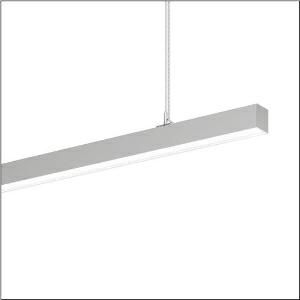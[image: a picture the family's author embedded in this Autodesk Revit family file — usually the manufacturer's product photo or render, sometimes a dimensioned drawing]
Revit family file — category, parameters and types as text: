
# Revit family: silica_21_51mx30tct9s
name_source: partatom
category: Lighting Fixtures
units: mm (PartAtom-declared; Revit-internal decimal feet)

## family parameters
Cut with Voids When Loaded = No
Host = Face
Light Source = No
Part Type = Normal
Room Calculation Point = No
Round Connector Dimension = Use Diameter
Shared = No

## types (1)
- --- (1 x LED, 10300 lm, 84.4 W, 6500K)
    Apparent Load = 84 VA
    CIE Flux Codes = 47 79 96 58 100
    Color Rendering = 80
    Color Temperature = 6500K
    Default Elevation = 1800 mm
    Description = Silica 21, office luminaire, primary optical cover: cover, of PMMA, opal, light emission: direct/indirect distribution, primary light characteristic: symmetric, installation type: suspended mounting, LED, rated luminous flux: 10.300lm, luminous efficacy: 116lm/W, light colour: 8tw, colour temperature: 2700..6500K, control gear: DALI DT8, with terminal, 3+2-pole, max. 2.5mm², mains connection: 220..240V, AC, 50/60Hz, rated input power: 88.7W, luminaire housing, of aluminium, metallic grey (RAL 9006), length: 3.004mm, width: 53mm, height: 53mm, protection rating (complete): IP20, insulation class (complete): insulation class I (protective earthing), certification: CE, permissible operating ambient temperature: 0..+35°C, standard: EN 50419, packaging unit: 1 piece
    Height = 53 mm
    Lamp = 1 x LED
    Lamp Light Flux = 10300 lm
    Lamp Power = 84.4 W
    Lamp count = 1
    Length = 3004 mm
    Luminous efficacy = 122 lm/W
    Manufacturer = Siteco
    ModVariant = No
    Model = 51MX30TCT9S
    Mounting Place = Ceiling
    Mounting Type = Pendant
    Number of Poles = 1
    OnlyDefault = Yes
    Power Factor = 1
    Product Name = Silica 21
    Product group = office luminaire | ceiling pendant
    ProductGroupID = 903
    Protection Class = Protection class I
    Protection Degree = IP 20
    RLX_Detail_Level = 1
    RLX_Emergency_Light_Flux = 0 lm
    RLX_Emergency_Type = 0
    RLX_Emergency_Type_DB = No
    RlxData = <blob elided: 20045 chars, md5=60dc22a9>
    Socket = socket
    Standby Power = 0 W
    System Light Flux = 10300 lm
    System Power = 84 W
    Type Comments = individual setting
    Type Image = l_1335864.jpg
    URL = http://relux.com
    VarID = @adj_140659
    Voltage = 0 V
    Weight = 0.00 kg
    Width = 53 mm

## geometry (parser evidence)
native form markers: Blend x4, Sweep x13
no freeform markers — native parametric forms only
